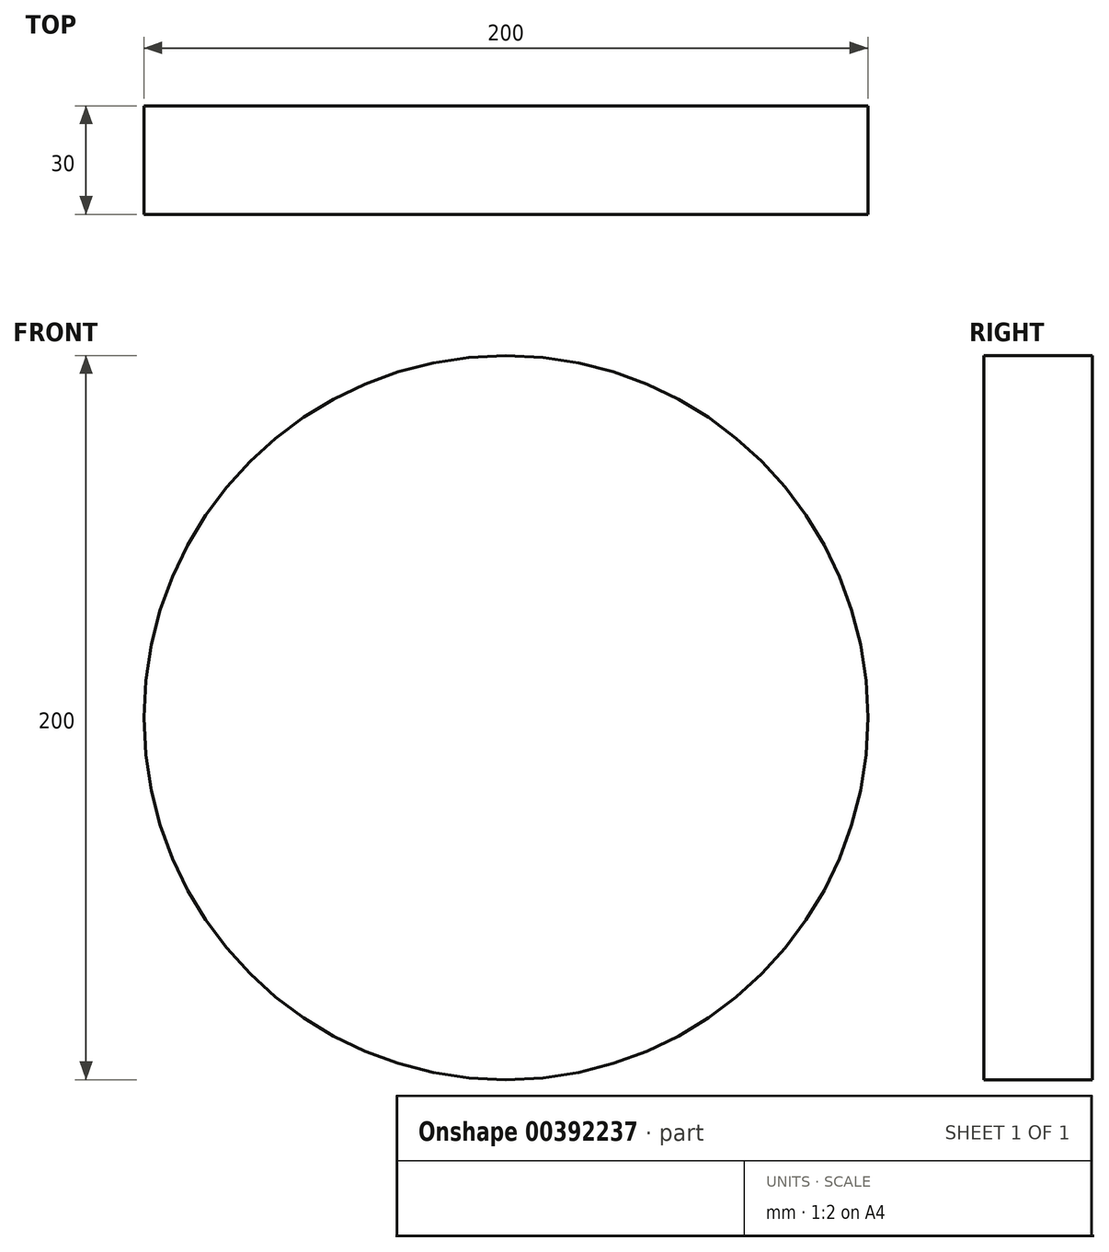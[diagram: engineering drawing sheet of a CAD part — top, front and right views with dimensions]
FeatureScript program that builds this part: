
annotation { "Feature Type Name" : "Feature", "Feature Type Description" : "" }
export const myFeature = defineFeature(function(context is Context, id is Id, definition is map)
    precondition{}
    {
        {
            var Q0;
            Q0=qCreatedBy(makeId("Front.planeOp"),FACE);
            var sketch = newSketch(context, id + "F0", { "sketchPlane" : qUnion([Q0])});
            skCircle(sketch, "E0", {"center": v(0, 0) * mm, "radius": 100 * mm});
            skSolve(sketch);
        }
        {
            var Q0;
            Q0 = qSketchRegion(id + "F0", true);
            extrude(context, id + "F1", {"entities" : qUnion([Q0]), "depth" : 30 * mm});
        }
        {
            var Q0;
            Q0=makeQuery(id+"F1.opExtrude","CAP_FACE",FACE,{"disambiguationData":[OSD([sQuery(id+"F0.wireOp",EDGE,"E0")])],"isStart":false});
            var sketch = newSketch(context, id + "F2", { "sketchPlane" : qUnion([Q0])});
            skLineSegment(sketch, "E1", {"start": v(0, 81.83) * mm, "end": v(-5, 81.83) * mm});
            skLineSegment(sketch, "E2", {"start": v(-5, 81.83) * mm, "end": v(-6.83, 87.18) * mm});
            skLineSegment(sketch, "E3", {"start": v(-6.83, 87.18) * mm, "end": v(-13.5, 97.83) * mm});
            skLineSegment(sketch, "E4", {"start": v(-13.5, 97.83) * mm, "end": v(0, 97.83) * mm});
            skLineSegment(sketch, "E5.MirrorCS", {"start": v(5, 81.83) * mm, "end": v(6.83, 87.18) * mm});
            skLineSegment(sketch, "E6.MirrorCS", {"start": v(6.83, 87.18) * mm, "end": v(13.5, 97.83) * mm});
            skLineSegment(sketch, "E7.MirrorCS", {"start": v(13.5, 97.83) * mm, "end": v(0, 97.83) * mm});
            skLineSegment(sketch, "E8.MirrorCS", {"start": v(0, 81.83) * mm, "end": v(5, 81.83) * mm});
            skSolve(sketch);
        }
        {
            var Q0;
            Q0=makeQuery(id+"F2.imprint","IMPRINT",FACE,{"disambiguationData":[TD([[makeQuery(id+"F2.imprint","IMPRINT",EDGE,{"derivedFrom":sQuery(id+"F2.wireOp",EDGE,"E1")}),-1.0]])]});
            extrude(context, id + "F3", {"entities" : qUnion([Q0]), "operationType" : NewBodyOperationType.ADD, "oppositeDirection" : true, "depth" : 30 * mm});
        }
    });
